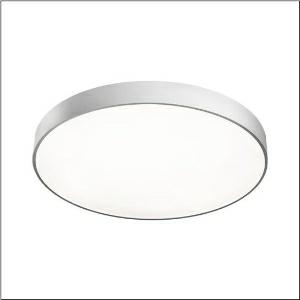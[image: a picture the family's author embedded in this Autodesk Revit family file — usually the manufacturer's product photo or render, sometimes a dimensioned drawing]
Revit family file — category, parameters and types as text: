
# Revit family: round_21_l_51mr38fd0321s
name_source: partatom
category: Lighting Fixtures
units: mm (PartAtom-declared; Revit-internal decimal feet)

## family parameters
Cut with Voids When Loaded = No
Host = Face
Light Source = No
Part Type = Normal
Room Calculation Point = No
Round Connector Dimension = Use Diameter
Shared = No

## types (1)
- Round 21 L (1 x LED, 13590 lm, 97 W, 3000K)
    Apparent Load = 97 VA
    CIE Flux Codes = 49 80 96 100 100
    Color Rendering = 80
    Color Temperature = 3000K
    Default Elevation = 1800 mm
    Description = Round 21 L, wall and ceiling luminaire, primary optical cover: cover, of PMMA, opal, light emission: direct distribution, primary light characteristic: symmetric, installation type: suspended mounting, surface-mounted, LED, rated luminous flux: 13.590lm, luminous efficacy: 140lm/W, light colour: 830, colour temperature: 3000K, control gear: DALI 2, with terminal, 5-pole, mains connection: 230V, AC, 50/60Hz, rated input power: 97W, housing, of aluminium, coated, silver, diameter: 850mm, height: 62mm, protection rating (complete): IP40, insulation class (complete): insulation class I (protective earthing), certification: CE, impact resistance: IK04, permissible operating ambient temperature: -10..+35°C, packaging unit: 1 piece
    Height = 87 mm
    Lamp = 1 x LED
    Lamp Light Flux = 13590 lm
    Lamp Power = 97 W
    Lamp count = 1
    Length = 850 mm
    Luminous efficacy = 140 lm/W
    Manufacturer = Siteco
    ModVariant = No
    Model = 51MR38FD0321S
    Mounting Place = Ceiling
    Mounting Type = Surface mounted
    Number of Poles = 1
    OnlyDefault = Yes
    Power Factor = 1
    Product Name = Round 21 L
    Product group = wall and ceiling luminaire | ceiling mounted
    ProductGroupID = 304
    Protection Class = Protection class I
    Protection Degree = IP 40
    RLX_Detail_Level = 1
    RLX_Emergency_Light_Flux = 0 lm
    RLX_Emergency_Type = 0
    RLX_Emergency_Type_DB = No
    RlxData = <blob elided: 20245 chars, md5=9f8b03a0>
    Socket = socket
    Standby Power = 0 W
    System Light Flux = 13590 lm
    System Power = 97 W
    Type Comments = Product without accessories
    Type Image = l_1258324.jpg
    URL = http://relux.com
    VarID = ---
    Voltage = 0 V
    Weight = 0.00 kg
    Width = 0 mm  [stored 0 ft]

note: [stored X ft] marks values corroborated as IEEE doubles in the binary element streams (Revit-internal decimal feet)

## geometry (parser evidence)
native form markers: Blend x4, Sweep x9
no freeform markers — native parametric forms only
